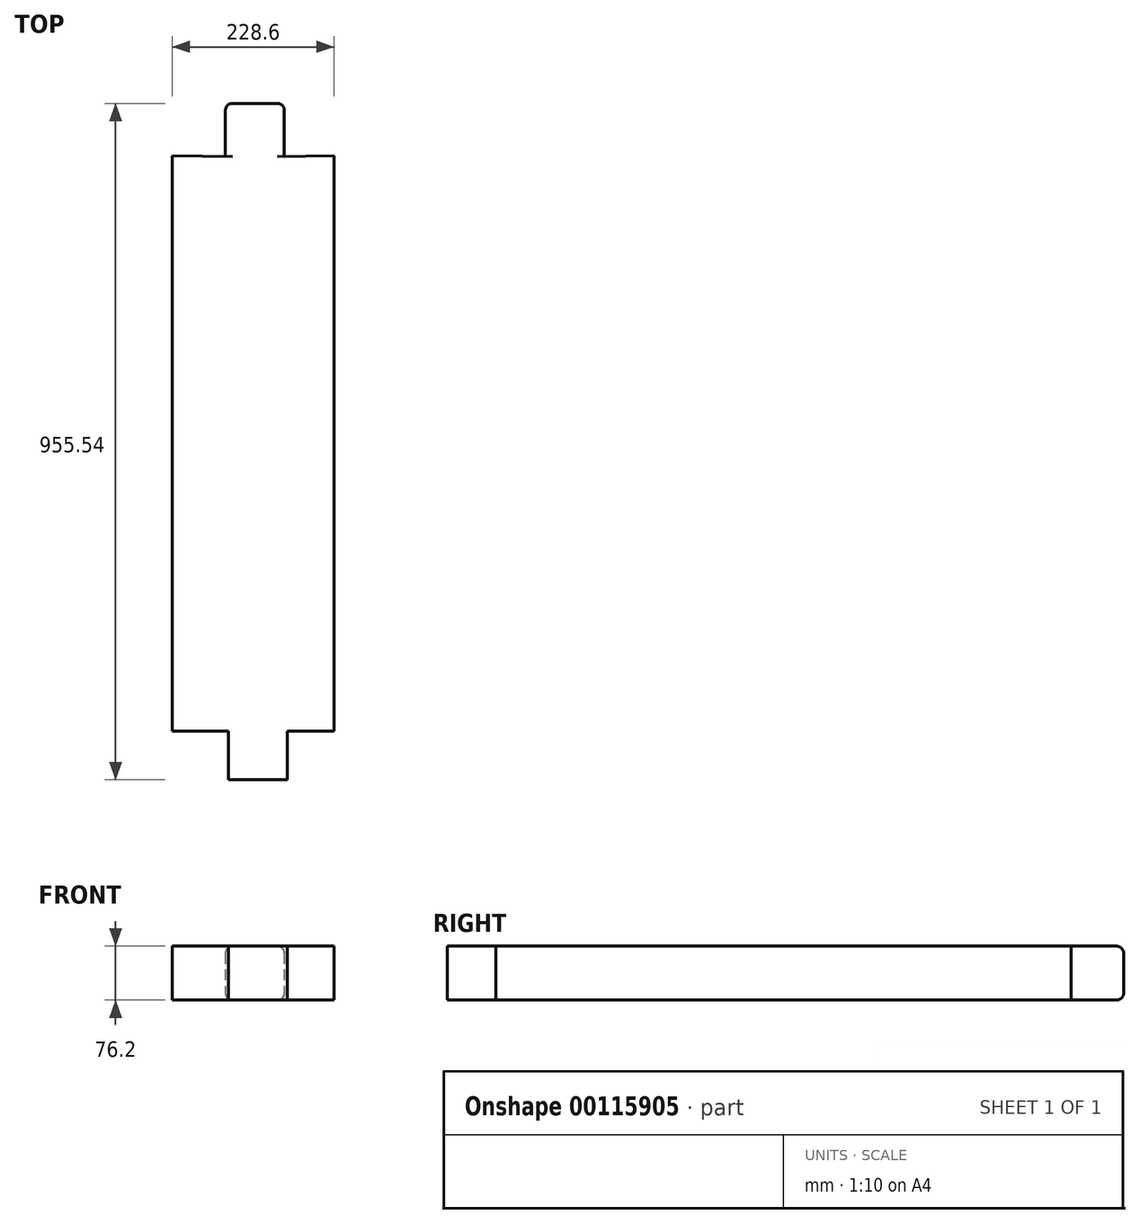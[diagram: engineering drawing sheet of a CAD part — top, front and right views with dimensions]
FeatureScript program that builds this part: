
annotation { "Feature Type Name" : "Feature", "Feature Type Description" : "" }
export const myFeature = defineFeature(function(context is Context, id is Id, definition is map)
    precondition{}
    {
        {
            var Q0;
            Q0=qCreatedBy(makeId("Top.planeOp"),FACE);
            var sketch = newSketch(context, id + "F0", { "sketchPlane" : qUnion([Q0])});
            skLineSegment(sketch, "E0.left", {"start": v(0, 812.8) * mm, "end": v(0, 0) * mm});
            skLineSegment(sketch, "E0.right", {"start": v(228.6, 812.8) * mm, "end": v(228.6, 0) * mm});
            skLineSegment(sketch, "E1", {"start": v(75.05, 886.85) * mm, "end": v(158.32, 886.85) * mm});
            skLineSegment(sketch, "E2", {"start": v(75.05, 886.85) * mm, "end": v(75.05, 811.9) * mm});
            skLineSegment(sketch, "E3", {"start": v(75.05, 811.9) * mm, "end": v(0, 812.8) * mm});
            skLineSegment(sketch, "E4", {"start": v(158.32, 886.85) * mm, "end": v(158.32, 811.9) * mm});
            skLineSegment(sketch, "E5", {"start": v(158.32, 811.9) * mm, "end": v(228.6, 812.8) * mm});
            skLineSegment(sketch, "E6", {"start": v(0, 0) * mm, "end": v(79.21, 0) * mm});
            skLineSegment(sketch, "E7", {"start": v(79.21, 0) * mm, "end": v(79.21, -68.69) * mm});
            skLineSegment(sketch, "E8", {"start": v(79.21, -68.69) * mm, "end": v(162.48, -68.69) * mm});
            skLineSegment(sketch, "E9", {"start": v(162.48, -68.69) * mm, "end": v(162.48, 0) * mm});
            skLineSegment(sketch, "E10", {"start": v(162.48, 0) * mm, "end": v(228.6, 0) * mm});
            skSolve(sketch);
        }
        {
            var Q0;
            Q0=qSketchRegion(id+"F0",true);
            extrude(context, id + "F1", {"entities" : qUnion([Q0]), "depth" : 76.2 * mm});
        }
        {
            var Q0;
            Q0=makeQuery(id+"F1.opExtrude","SWEPT_EDGE",EDGE,{"disambiguationData":[OSD([sQuery(id+"F0.wireOp",EDGE,"E1"),sQuery(id+"F0.wireOp",EDGE,"E2")])]});
            var Q1;
            Q1=makeQuery(id+"F1.opExtrude","CAP_EDGE",EDGE,{"disambiguationData":[OSD([sQuery(id+"F0.wireOp",EDGE,"E1")])],"isStart":false});
            var Q2;
            Q2=makeQuery(id+"F1.opExtrude","CAP_EDGE",EDGE,{"disambiguationData":[OSD([sQuery(id+"F0.wireOp",EDGE,"E2")])],"isStart":false});
            var Q3;
            Q3=makeQuery(id+"F1.opExtrude","CAP_EDGE",EDGE,{"disambiguationData":[OSD([sQuery(id+"F0.wireOp",EDGE,"E4")])],"isStart":false});
            var Q4;
            Q4=makeQuery(id+"F1.opExtrude","SWEPT_EDGE",EDGE,{"disambiguationData":[OSD([sQuery(id+"F0.wireOp",EDGE,"E1"),sQuery(id+"F0.wireOp",EDGE,"E4")])]});
            var Q5;
            Q5=makeQuery(id+"F1.opExtrude","CAP_EDGE",EDGE,{"disambiguationData":[OSD([sQuery(id+"F0.wireOp",EDGE,"E1")])],"isStart":true});
            var Q6;
            Q6=makeQuery(id+"F1.opExtrude","CAP_EDGE",EDGE,{"disambiguationData":[OSD([sQuery(id+"F0.wireOp",EDGE,"E2")])],"isStart":true});
            var Q7;
            Q7=makeQuery(id+"F1.opExtrude","CAP_EDGE",EDGE,{"disambiguationData":[OSD([sQuery(id+"F0.wireOp",EDGE,"E4")])],"isStart":true});
            fillet(context, id + "F2", {"entities" : qUnion([Q0, Q1, Q2, Q3, Q4, Q5, Q6, Q7]), "radius" : 10 * mm, "tangentPropagation" : true, "allowEdgeOverflow" : false});
        }
    });
